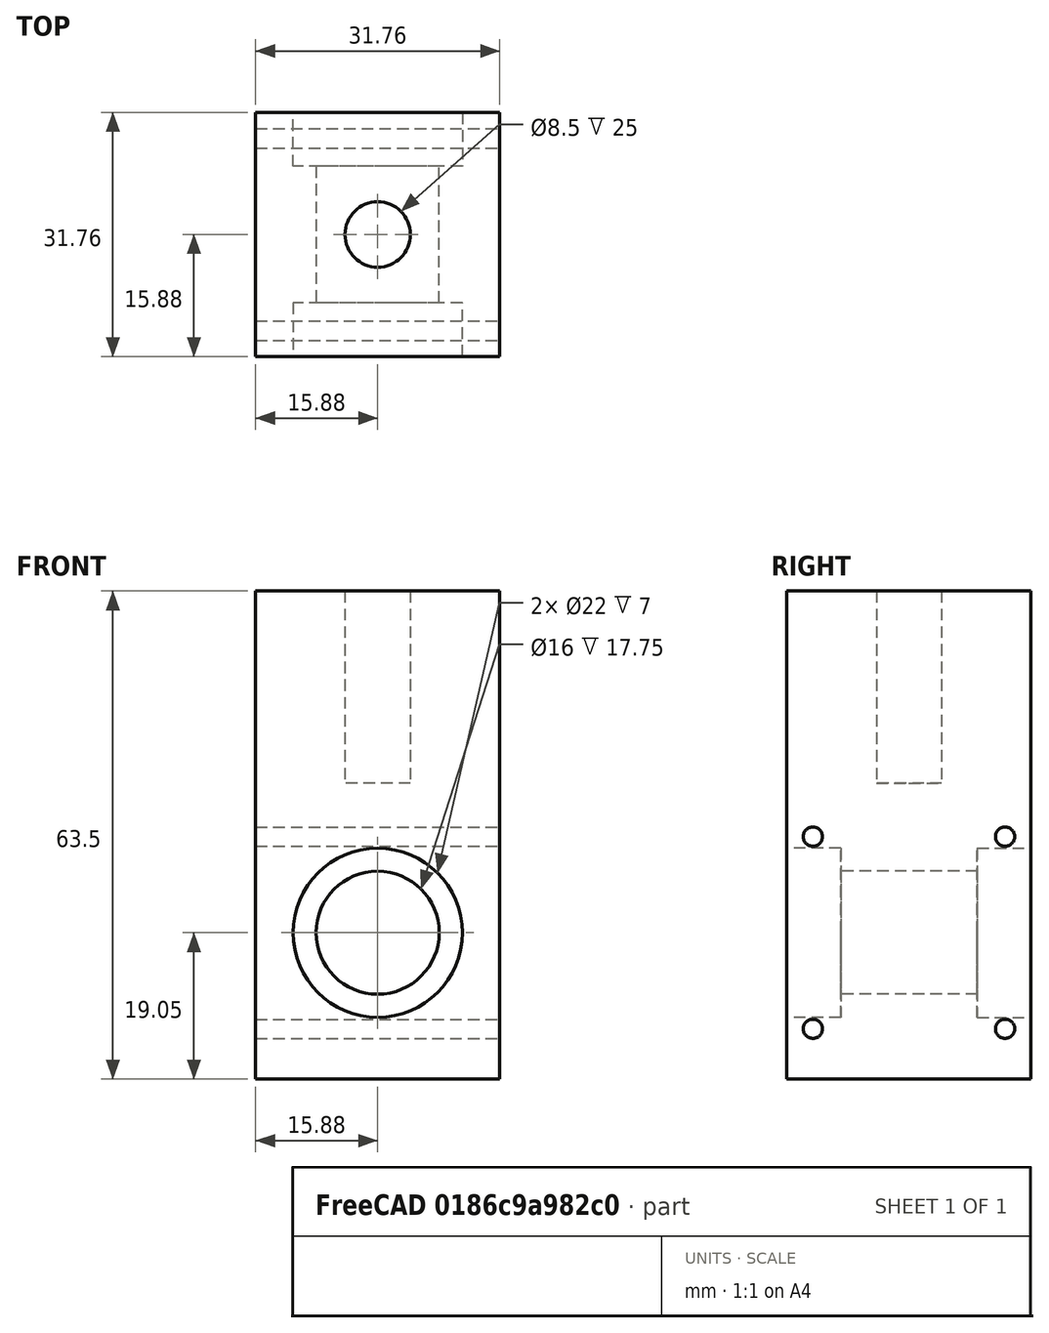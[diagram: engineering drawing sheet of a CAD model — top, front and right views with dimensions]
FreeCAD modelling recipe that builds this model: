
FCSTD DOCUMENT  (FreeCAD 0.21R33771 (Git))
Label: Lower Bearing Block
License: All rights reserved
LicenseURL: http://en.wikipedia.org/wiki/All_rights_reserved
objects: TechDraw::DrawViewDimension×8, Sketcher::SketchObject×5, PartDesign::CoordinateSystem×4, TechDraw::DrawProjGroupItem×4, PartDesign::Pocket×2, PartDesign::Hole×2, TechDraw::DrawViewBalloon×2, PartDesign::Pad×1, PartDesign::Mirrored×1, TechDraw::DrawSVGTemplate×1, TechDraw::DrawViewAnnotation×1, PartDesign::Body×1, TechDraw::DrawProjGroup×1, TechDraw::DrawPage×1
note: 21 computed .brp shape members not serialized (recipe doc carries the construction recipe); baked Part::Feature solids carry a one-line shape summary decoded from their .brp

FEATURE [Sketcher::SketchObject] Sketch
  FullyConstrained = true
  MapMode = 5
  Support = -> [XY_Plane]
  sketch-geometry (5):
    g0: LineSegment StartX=-15.875 StartY=15.875 StartZ=0 EndX=-15.875 EndY=-15.875 EndZ=0
    g1: LineSegment StartX=-15.875 StartY=-15.875 StartZ=0 EndX=15.875 EndY=-15.875 EndZ=0
    g2: LineSegment StartX=15.875 StartY=-15.875 StartZ=0 EndX=15.875 EndY=15.875 EndZ=0
    g3: LineSegment StartX=15.875 StartY=15.875 StartZ=0 EndX=-15.875 EndY=15.875 EndZ=0
    g4: GeomPoint X=-1e-16 Y=0 Z=0
  constraints (12):
    c: Coincident(g0,g1)
    c: Coincident(g1,g2)
    c: Coincident(g2,g3)
    c: Coincident(g3,g0)
    c: Horizontal(g1)
    c: Horizontal(g3)
    c: Vertical(g0)
    c: Vertical(g2)
    c: Symmetric(g1,g0,g4)
    c: Coincident(g4,g-1)
    c: Equal(g2,g3)
    c: DistanceY(g2,g2) = 31.75
FEATURE [PartDesign::Pad] Pad
  Direction = (0,0,1)
  Length = 63.5
  Length2 = 10
  Profile = -> Sketch
  ReferenceAxis = -> Sketch [N_Axis]
  Type = 0
FEATURE [Sketcher::SketchObject] Sketch001
  FullyConstrained = true
  MapMode = 5
  Placement = pos=(0,-15.875,0) rot=(1,0,0;1.5708rad)
  Support = -> [Pad]
  sketch-geometry (1):
    g0: Circle CenterX=0 CenterY=19.05 CenterZ=0 NormalX=0 NormalY=0 NormalZ=1 AngleXU=0 Radius=11
  constraints (3):
    c: PointOnObject(g0,g-2)
    c: DistanceY(g-1,g0) = 19.05
    c: Diameter(g0) = 22
FEATURE [PartDesign::Pocket] Pocket
  BaseFeature = -> Pad
  Direction = (1,1,1)
  Length = 7
  Length2 = 5
  Profile = -> Sketch001
  Type = 0
FEATURE [PartDesign::Mirrored] Mirrored
  BaseFeature = -> Pocket
  MirrorPlane = -> XZ_Plane
  Originals = -> [Pocket]
FEATURE [Sketcher::SketchObject] Sketch002
  FullyConstrained = true
  MapMode = 5
  Placement = pos=(0,-15.875,0) rot=(1,0,0;1.5708rad)
  Support = -> [Mirrored]
  sketch-geometry (1):
    g0: Circle CenterX=0 CenterY=19.05 CenterZ=0 NormalX=0 NormalY=0 NormalZ=1 AngleXU=0 Radius=8
  constraints (3):
    c: PointOnObject(g0,g-2)
    c: DistanceY(g-1,g0) = 19.05
    c: Diameter(g0) = 16
FEATURE [PartDesign::Pocket] Pocket001
  BaseFeature = -> Mirrored
  Direction = (1,1,1)
  Length = 5
  Length2 = 5
  Profile = -> Sketch002
  Type = 1
FEATURE [Sketcher::SketchObject] Sketch003
  FullyConstrained = true
  MapMode = 5
  Placement = pos=(-15.875,0,0) rot=(0.57735,-0.57735,-0.57735;2.0944rad)
  Support = -> [Pocket001]
  sketch-geometry (9):
    g0: LineSegment StartX=-12.5 StartY=31.55 StartZ=0 EndX=-12.5 EndY=6.55 EndZ=0
    g1: LineSegment StartX=-12.5 StartY=6.55 StartZ=0 EndX=12.5 EndY=6.55 EndZ=0
    g2: LineSegment StartX=12.5 StartY=6.55 StartZ=0 EndX=12.5 EndY=31.55 EndZ=0
    g3: LineSegment StartX=12.5 StartY=31.55 StartZ=0 EndX=-12.5 EndY=31.55 EndZ=0
    g4: GeomPoint X=0 Y=19.05 Z=0
    g5: Circle CenterX=12.5 CenterY=31.55 CenterZ=0 NormalX=0 NormalY=0 NormalZ=1 AngleXU=0 Radius=1.25
    g6: Circle CenterX=12.5 CenterY=6.55 CenterZ=0 NormalX=0 NormalY=0 NormalZ=1 AngleXU=0 Radius=1.25
    g7: Circle CenterX=-12.5 CenterY=6.55 CenterZ=0 NormalX=0 NormalY=0 NormalZ=1 AngleXU=0 Radius=1.25
    g8: Circle CenterX=-12.5 CenterY=31.55 CenterZ=0 NormalX=0 NormalY=0 NormalZ=1 AngleXU=0 Radius=1.25
  constraints (21):
    c: Coincident(g0,g1)
    c: Coincident(g1,g2)
    c: Coincident(g2,g3)
    c: Coincident(g3,g0)
    c: Horizontal(g1)
    c: Horizontal(g3)
    c: Vertical(g0)
    c: Vertical(g2)
    c: Symmetric(g1,g0,g4)
    c: PointOnObject(g4,g-2)
    c: Equal(g2,g3)
    c: DistanceY(g-1,g4) = 19.05
    c: DistanceY(g2,g2) = 25
    c: Coincident(g5,g2)
    c: Coincident(g6,g1)
    c: Coincident(g7,g0)
    c: Coincident(g8,g0)
    c: Equal(g8,g5)
    c: Equal(g5,g6)
    c: Equal(g6,g7)
    c: Diameter(g5) = 2.5
FEATURE [PartDesign::Hole] Hole
  BaseFeature = -> Pocket001
  CustomThreadClearance = 0
  Depth = 157.098
  DepthType = 1
  Diameter = 2.5
  DrillForDepth = false
  DrillPoint = 1
  DrillPointAngle = 118
  HoleCutCountersinkAngle = 90
  HoleCutCustomValues = false
  HoleCutDepth = 0
  HoleCutDiameter = 6.1
  HoleCutType = 0
  ModelThread = false
  Profile = -> Sketch003
  Tapered = false
  TaperedAngle = 90
  ThreadClass = 0
  ThreadDepth = 157.098
  ThreadDepthType = 0
  ThreadDirection = 0
  ThreadFit = 0
  ThreadSize = 9
  ThreadType = 1
  Threaded = true
  UseCustomThreadClearance = false
FEATURE [Sketcher::SketchObject] Sketch004
  FullyConstrained = true
  MapMode = 5
  Placement = pos=(0,0,63.5) rot=(0,0,1;0rad)
  Support = -> [Hole]
  sketch-geometry (1):
    g0: Circle CenterX=0 CenterY=0 CenterZ=0 NormalX=0 NormalY=0 NormalZ=1 AngleXU=0 Radius=4.25
  constraints (2):
    c: Coincident(g0,g-1)
    c: Diameter(g0) = 8.5
FEATURE [PartDesign::Hole] Hole001
  BaseFeature = -> Hole
  CustomThreadClearance = 0
  Depth = 25
  DepthType = 0
  Diameter = 8.5
  DrillForDepth = false
  DrillPoint = 0
  DrillPointAngle = 118
  HoleCutCountersinkAngle = 90
  HoleCutCustomValues = false
  HoleCutDepth = 0
  HoleCutDiameter = 0
  HoleCutType = 0
  ModelThread = false
  Profile = -> Sketch004
  Tapered = false
  TaperedAngle = 90
  ThreadClass = 0
  ThreadDepth = 25
  ThreadDepthType = 0
  ThreadDirection = 0
  ThreadFit = 0
  ThreadSize = 18
  ThreadType = 1
  Threaded = true
  UseCustomThreadClearance = false
FEATURE [TechDraw::DrawSVGTemplate] Template
  EditableTexts = Designed_by_Name=RIO LIU; FC-Date=2022-12-13; FC-SC=1:1; FC-SH=1; FC-Title=LOWER BEARING BLOCK
  Height = 210
  Orientation = 1
  Width = 297
FEATURE [TechDraw::DrawViewAnnotation] Annotation
  Font = osifont
  LineSpace = 80
  LockPosition = false
  MaxWidth = -1
  Rotation = 0
  ScaleType = 0
  Text = ALL UNIT IN mm UNLESS SPECIFIED
  TextSize = 5
  TextStyle = 0
  X = 77.4616
  Y = 30.7838
FEATURE [PartDesign::CoordinateSystem] Local_CS
  AttacherType = Attacher::AttachEngine3D
  MapMode = 45
  Placement = pos=(0,12.375,19.05) rot=(0,0.707107,0.707107;3.14159rad)
  Support = -> [Hole001]
FEATURE [PartDesign::CoordinateSystem] Local_CS001
  AttacherType = Attacher::AttachEngine3D
  MapMode = 45
  Placement = pos=(0,-12.375,19.05) rot=(0,0.707107,0.707107;3.14159rad)
  Support = -> [Hole001]
FEATURE [PartDesign::CoordinateSystem] Local_CS002
  AttacherType = Attacher::AttachEngine3D
  MapMode = 5
  Placement = pos=(0,0,38.5) rot=(0,0,1;0rad)
  Support = -> [Hole001]
FEATURE [PartDesign::CoordinateSystem] Local_CS003
  AttacherType = Attacher::AttachEngine3D
  MapMode = 45
  Placement = pos=(0,-3.9e-15,19.05) rot=(0,0.707107,0.707107;3.14159rad)
  Support = -> [Hole001]
FEATURE [PartDesign::Body] Body  label="Lower Bearing Block"
  Group = -> [Sketch,Pad,Sketch001,Pocket,Mirrored,Sketch002,Pocket001,Sketch003,Hole,Sketch004,Hole001,Local_CS,Local_CS001,Local_CS002,Local_CS003]
  Origin = -> Origin
  Tip = -> Hole001
FEATURE [TechDraw::DrawProjGroupItem] ProjItem  label="Front"
  CoarseView = false
  Direction = (1e-16,0,1)
  Focus = 100
  HardHidden = false
  IsoCount = 0
  IsoHidden = false
  IsoVisible = false
  LockPosition = true
  Perspective = false
  Rotation = 0
  RotationVector = (0,0,-1)
  ScaleType = 2
  ScrubCount = 0
  SeamHidden = false
  SeamVisible = true
  SmoothHidden = false
  SmoothVisible = true
  Source = -> [Body]
  Type = 0
  X = 0
  XDirection = (1e-16,-1,0)
  Y = 0
FEATURE [TechDraw::DrawProjGroupItem] ProjItem003  label="Left"
  CoarseView = false
  Direction = (-1e-16,1,1e-16)
  Focus = 100
  HardHidden = false
  IsoCount = 0
  IsoHidden = false
  IsoVisible = false
  LockPosition = false
  Perspective = false
  Rotation = 0
  RotationVector = (1,0,0)
  ScaleType = 2
  ScrubCount = 0
  SeamHidden = false
  SeamVisible = true
  SmoothHidden = false
  SmoothVisible = true
  Source = -> [Body]
  Type = 1
  X = -122.546
  XDirection = (1e-16,-1e-16,1)
  Y = 0
FEATURE [TechDraw::DrawProjGroupItem] ProjItem005  label="FrontTopLeft"
  CoarseView = false
  Direction = (0.57735,0.57735,0.57735)
  Focus = 100
  HardHidden = false
  IsoCount = 0
  IsoHidden = false
  IsoVisible = false
  LockPosition = false
  Perspective = false
  Rotation = 0
  RotationVector = (1,0,0)
  ScaleType = 2
  ScrubCount = 0
  SeamHidden = false
  SeamVisible = true
  SmoothHidden = false
  SmoothVisible = true
  Source = -> [Body]
  Type = 6
  X = -126.729
  XDirection = (1e-16,-0.707107,0.707107)
  Y = 84.3257
FEATURE [TechDraw::DrawProjGroupItem] ProjItem004  label="Top"
  CoarseView = false
  Direction = (1,1e-16,-1e-16)
  Focus = 100
  HardHidden = true
  IsoCount = 0
  IsoHidden = false
  IsoVisible = false
  LockPosition = false
  Perspective = false
  Rotation = 0
  RotationVector = (1,0,0)
  ScaleType = 2
  ScrubCount = 0
  SeamHidden = false
  SeamVisible = true
  SmoothHidden = false
  SmoothVisible = true
  Source = -> [Body]
  Type = 4
  X = 0
  XDirection = (1e-16,-1,0)
  Y = 59.4872
FEATURE [TechDraw::DrawProjGroup] ProjGroup
  Anchor = -> ProjItem
  AutoDistribute = false
  LockPosition = false
  ProjectionType = 1
  Rotation = 0
  ScaleType = 0
  Source = -> [Body]
  Views = -> [ProjItem,ProjItem003,ProjItem004,ProjItem005]
  X = 207.977
  Y = 78.5486
  spacingX = 15
  spacingY = 15
FEATURE [TechDraw::DrawViewDimension] Dimension
  AngleOverride = false
  Arbitrary = false
  ArbitraryTolerances = false
  EqualTolerance = true
  ExtensionAngle = 0
  FormatSpec = %.2f (2 1/2")
  FormatSpecOverTolerance = %+.2w
  FormatSpecUnderTolerance = %+.2w
  Inverted = false
  LineAngle = 0
  LockPosition = false
  MeasureType = 1
  OverTolerance = 0
  References2D = -> [ProjItem004]
  Rotation = 0
  ScaleType = 0
  TheoreticalExact = false
  Type = 2
  UnderTolerance = 0
  X = -58.8937
  Y = 2.80243
FEATURE [TechDraw::DrawViewBalloon] Balloon
  BubbleShape = 1
  EndType = 0
  EndTypeScale = 1
  KinkLength = 5
  LockPosition = false
  OriginX = 12.5
  OriginY = 26.4801
  Rotation = 0
  ScaleType = 0
  ShapeScale = 1
  SourceView = -> ProjItem004
  Text = M3 THRU TYP
  TextWrapLen = -1
  X = 43.3115
  Y = 36.2696
FEATURE [TechDraw::DrawViewDimension] Dimension014
  AngleOverride = false
  Arbitrary = false
  ArbitraryTolerances = false
  EqualTolerance = true
  ExtensionAngle = 0
  FormatSpec = %.1f (3/4")
  FormatSpecOverTolerance = %+.1f
  FormatSpecUnderTolerance = %+.1f
  Inverted = false
  LineAngle = 0
  LockPosition = false
  MeasureType = 1
  OverTolerance = 0
  References2D = -> [ProjItem003]
  Rotation = 0
  ScaleType = 0
  TheoreticalExact = false
  Type = 1
  UnderTolerance = 0
  X = 13.744
  Y = -20.9072
FEATURE [TechDraw::DrawViewDimension] Dimension015
  AngleOverride = false
  Arbitrary = false
  ArbitraryTolerances = false
  EqualTolerance = true
  ExtensionAngle = 0
  FormatSpec = %.1f TYP
  FormatSpecOverTolerance = %+.1f
  FormatSpecUnderTolerance = %+.1f
  Inverted = false
  LineAngle = 0
  LockPosition = false
  MeasureType = 1
  OverTolerance = 0
  References2D = -> [ProjItem004]
  Rotation = 0
  ScaleType = 0
  TheoreticalExact = false
  Type = 1
  UnderTolerance = 0
  X = -32.7087
  Y = 45.9095
FEATURE [TechDraw::DrawViewDimension] Dimension016
  AngleOverride = false
  Arbitrary = false
  ArbitraryTolerances = false
  EqualTolerance = true
  ExtensionAngle = 0
  FormatSpec = ⌀%.1f
  FormatSpecOverTolerance = %+.1f
  FormatSpecUnderTolerance = %+.1f
  Inverted = false
  LineAngle = 0
  LockPosition = false
  MeasureType = 1
  OverTolerance = 0
  References2D = -> [ProjItem003]
  Rotation = 0
  ScaleType = 0
  TheoreticalExact = false
  Type = 5
  UnderTolerance = 0
  X = -44.2485
  Y = -4.00525
FEATURE [TechDraw::DrawViewDimension] Dimension017
  AngleOverride = false
  Arbitrary = false
  ArbitraryTolerances = false
  EqualTolerance = true
  ExtensionAngle = 0
  FormatSpec = ⌀%.1f
  FormatSpecOverTolerance = %+.1f
  FormatSpecUnderTolerance = %+.1f
  Inverted = false
  LineAngle = 0
  LockPosition = false
  MeasureType = 1
  OverTolerance = 0
  References2D = -> [ProjItem003]
  Rotation = 0
  ScaleType = 0
  TheoreticalExact = false
  Type = 5
  UnderTolerance = 0
  X = -44.63
  Y = -11.825
FEATURE [TechDraw::DrawViewDimension] Dimension019
  AngleOverride = false
  Arbitrary = false
  ArbitraryTolerances = false
  EqualTolerance = true
  ExtensionAngle = 0
  FormatSpec = %.1f
  FormatSpecOverTolerance = %+.1f
  FormatSpecUnderTolerance = %+.1f
  Inverted = false
  LineAngle = 0
  LockPosition = false
  MeasureType = 1
  OverTolerance = 0
  References2D = -> [ProjItem004]
  Rotation = 0
  ScaleType = 0
  TheoreticalExact = false
  Type = 1
  UnderTolerance = 0
  X = -18.4038
  Y = 57.3125
FEATURE [TechDraw::DrawViewBalloon] Balloon001
  BubbleShape = 1
  EndType = 0
  EndTypeScale = 1
  KinkLength = 5
  LockPosition = false
  OriginX = 0
  OriginY = 4.25
  Rotation = 0
  ScaleType = 0
  ShapeScale = 1
  SourceView = -> ProjItem
  Text = M10 ↓25
  TextWrapLen = -1
  X = 37.8461
  Y = 14.8191
FEATURE [TechDraw::DrawViewDimension] Dimension020
  AngleOverride = false
  Arbitrary = false
  ArbitraryTolerances = false
  EqualTolerance = true
  ExtensionAngle = 0
  FormatSpec = %.1f
  FormatSpecOverTolerance = %+.1f
  FormatSpecUnderTolerance = %+.1f
  Inverted = false
  LineAngle = 0
  LockPosition = false
  MeasureType = 1
  OverTolerance = 0
  References2D = -> [ProjItem004]
  Rotation = 0
  ScaleType = 0
  TheoreticalExact = false
  Type = 2
  UnderTolerance = 0
  X = 28.7436
  Y = 26.4498
FEATURE [TechDraw::DrawViewDimension] Dimension021
  AngleOverride = false
  Arbitrary = false
  ArbitraryTolerances = false
  EqualTolerance = true
  ExtensionAngle = 0
  FormatSpec = %.1f (3/4")
  FormatSpecOverTolerance = %+.1f
  FormatSpecUnderTolerance = %+.1f
  Inverted = false
  LineAngle = 0
  LockPosition = false
  MeasureType = 1
  OverTolerance = 0
  References2D = -> [ProjItem004]
  Rotation = 0
  ScaleType = 0
  TheoreticalExact = false
  Type = 2
  UnderTolerance = 0
  X = -37.0051
  Y = 23.5067
FEATURE [TechDraw::DrawPage] Page
  KeepUpdated = true
  NextBalloonIndex = 6
  ProjectionType = 0
  Template = -> Template
  Views = -> [ProjGroup,Dimension,Balloon,Annotation,Dimension014,Dimension015,Dimension016,Dimension017,Dimension019,Balloon001,Dimension020,Dimension021]
